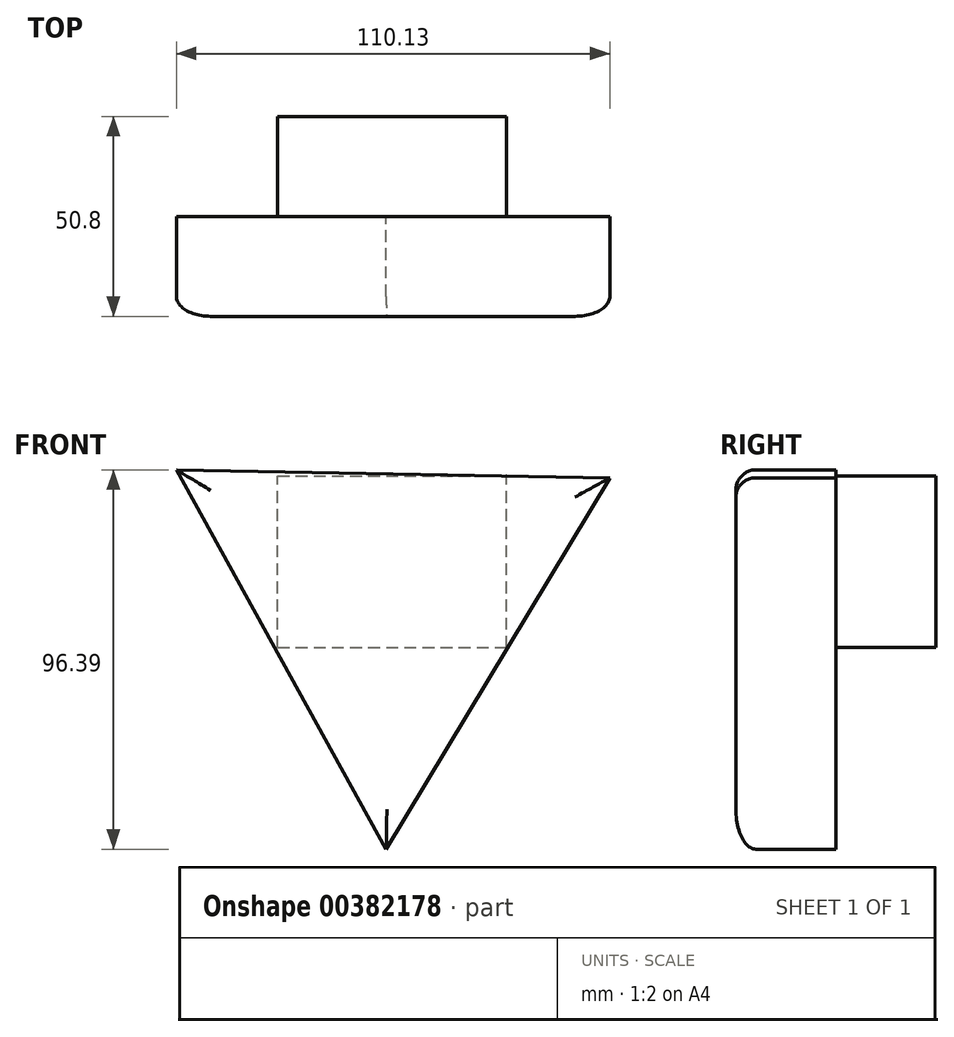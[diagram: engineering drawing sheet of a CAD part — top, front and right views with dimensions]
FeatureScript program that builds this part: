
annotation { "Feature Type Name" : "Feature", "Feature Type Description" : "" }
export const myFeature = defineFeature(function(context is Context, id is Id, definition is map)
    precondition{}
    {
        {
            var Q0;
            Q0=qCreatedBy(makeId("Front.planeOp"),FACE);
            var sketch = newSketch(context, id + "F0", { "sketchPlane" : qUnion([Q0])});
            skCircle(sketch, "E0.cCircle", {"center": v(-35.28, 32.03) * mm, "radius": 31.8 * mm, "construction": true});
            skLineSegment(sketch, "E0.0", {"start": v(20.37, 62.8) * mm, "end": v(-36.46, -31.55) * mm});
            skLineSegment(sketch, "E0.1", {"start": v(-36.46, -31.55) * mm, "end": v(-89.76, 64.84) * mm});
            skLineSegment(sketch, "E0.2", {"start": v(-89.76, 64.84) * mm, "end": v(20.37, 62.8) * mm});
            skPoint(sketch, "E0.0.midPoint", {"position": v(-8.05, 15.63) * mm});
            skSolve(sketch);
        }
        {
            var Q0;
            Q0=makeQuery(id+"F0.imprint","IMPRINT",FACE,{"disambiguationData":[TD([[makeQuery(id+"F0.imprint","IMPRINT",EDGE,{"derivedFrom":sQuery(id+"F0.wireOp",EDGE,"E0.0")}),-1.0]])]});
            extrude(context, id + "F1", {"entities" : qUnion([Q0]), "depth" : 25.4 * mm});
        }
        {
            var Q0;
            Q0=qCreatedBy(makeId("Front.planeOp"),FACE);
            var sketch = newSketch(context, id + "F2", { "sketchPlane" : qUnion([Q0])});
            skLineSegment(sketch, "E1.bottom", {"start": v(-64.04, 19.65) * mm, "end": v(-5.85, 19.65) * mm});
            skLineSegment(sketch, "E1.top", {"start": v(-64.04, 63.3) * mm, "end": v(-5.85, 63.3) * mm});
            skLineSegment(sketch, "E1.left", {"start": v(-64.04, 19.65) * mm, "end": v(-64.04, 63.3) * mm});
            skLineSegment(sketch, "E1.right", {"start": v(-5.85, 19.65) * mm, "end": v(-5.85, 63.3) * mm});
            skSolve(sketch);
        }
        {
            var Q0;
            Q0 = qSketchRegion(id + "F2", true);
            var Q1;
            Q1=makeQuery(id+"F1.opExtrude","CAP_FACE",FACE,{"disambiguationData":[OSD([sQuery(id+"F0.wireOp",EDGE,"E0.0"),sQuery(id+"F0.wireOp",EDGE,"E0.1"),sQuery(id+"F0.wireOp",EDGE,"E0.2")])],"isStart":false});
            extrude(context, id + "F3", {"entities" : qUnion([Q0, Q1]), "operationType" : NewBodyOperationType.ADD, "oppositeDirection" : true, "depth" : 25.4 * mm});
        }
        {
            var Q0;
            Q0=makeQuery(id+"F1.opExtrude","CAP_FACE",FACE,{"disambiguationData":[OSD([sQuery(id+"F0.wireOp",EDGE,"E0.0"),sQuery(id+"F0.wireOp",EDGE,"E0.1"),sQuery(id+"F0.wireOp",EDGE,"E0.2")])],"isStart":false});
            fillet(context, id + "F4", {"entities" : qUnion([Q0]), "radius" : 5.08 * mm, "tangentPropagation" : true, "allowEdgeOverflow" : false});
        }
    });
